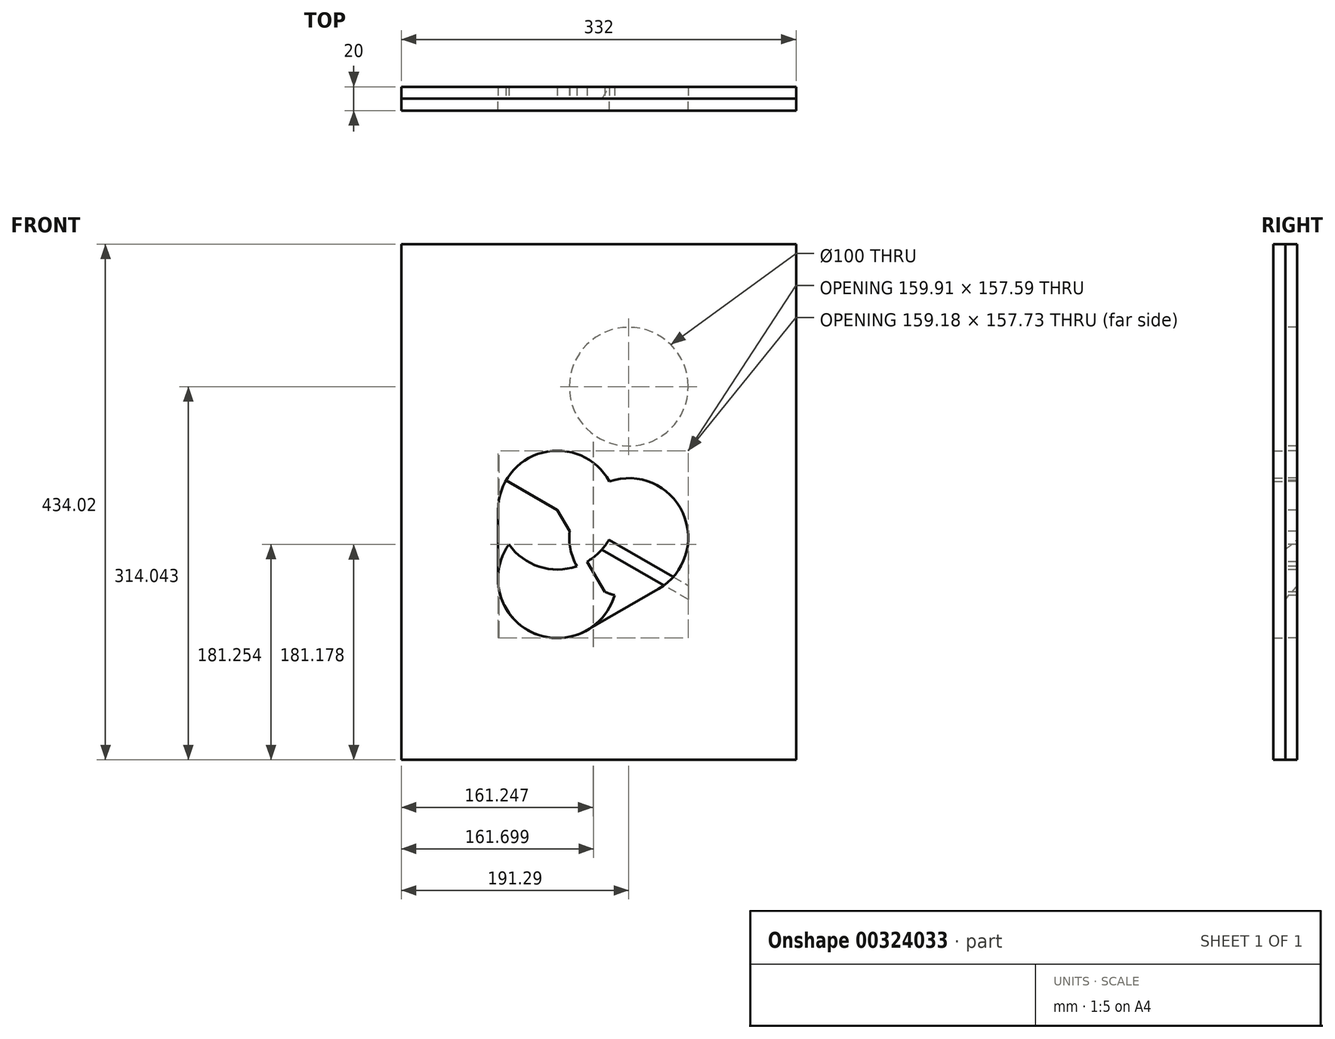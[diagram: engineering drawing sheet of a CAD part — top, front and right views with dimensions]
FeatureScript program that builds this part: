
annotation { "Feature Type Name" : "Feature", "Feature Type Description" : "" }
export const myFeature = defineFeature(function(context is Context, id is Id, definition is map)
    precondition{}
    {
        {
            var Q0;
            Q0=qCreatedBy(makeId("Front.planeOp"),FACE);
            var sketch = newSketch(context, id + "F0", { "sketchPlane" : qUnion([Q0])});
            skCircle(sketch, "E0", {"center": v(0, 0) * mm, "radius": 50 * mm});
            skCircle(sketch, "E1", {"center": v(0, -57.74) * mm, "radius": 50 * mm});
            skCircle(sketch, "E2", {"center": v(60, -23.1) * mm, "radius": 50 * mm});
            skLineSegment(sketch, "E3", {"start": v(0, 0) * mm, "end": v(50, -86.6) * mm});
            skLineSegment(sketch, "E4", {"start": v(50, -86.6) * mm, "end": v(85, -66.4) * mm});
            skLineSegment(sketch, "E5", {"start": v(50, -86.6) * mm, "end": v(25, -101.04) * mm});
            skLineSegment(sketch, "E6", {"start": v(-50, 0) * mm, "end": v(-50, -57.74) * mm});
            skLineSegment(sketch, "E7", {"start": v(-50, -57.74) * mm, "end": v(50, -57.74) * mm, "construction": true});
            skLineSegment(sketch, "E8", {"start": v(93.3, -61.6) * mm, "end": v(43.3, 25) * mm, "construction": true});
            skLineSegment(sketch, "E9", {"start": v(35, 20.2) * mm, "end": v(43.3, 25) * mm});
            skLineSegment(sketch, "E10", {"start": v(0, 0) * mm, "end": v(43.3, 25) * mm});
            skLineSegment(sketch, "E11", {"start": v(0, 0) * mm, "end": v(-43.3, 25) * mm});
            skLineSegment(sketch, "E12", {"start": v(-43.3, 25) * mm, "end": v(16.7, 128.92) * mm});
            skCircle(sketch, "E13", {"center": v(60, 103.92) * mm, "radius": 50 * mm});
            skLineSegment(sketch, "E14", {"start": v(0, 0) * mm, "end": v(43.3, -25) * mm});
            skLineSegment(sketch, "E15", {"start": v(43.3, -25) * mm, "end": v(110, -63.5) * mm});
            skLineSegment(sketch, "E16", {"start": v(110, 103.92) * mm, "end": v(110, -63.5) * mm});
            skLineSegment(sketch, "E17.bottom", {"start": v(-131.3, 223.9) * mm, "end": v(200.71, 223.9) * mm});
            skLineSegment(sketch, "E17.top", {"start": v(-131.3, -210.12) * mm, "end": v(200.71, -210.12) * mm});
            skLineSegment(sketch, "E17.left", {"start": v(-131.3, 223.9) * mm, "end": v(-131.3, -210.12) * mm});
            skLineSegment(sketch, "E17.right", {"start": v(200.71, 223.9) * mm, "end": v(200.71, -210.12) * mm});
            skSolve(sketch);
        }
        {
            var Q0;
            {var subQ5=sQuery(id+"F0.wireOp",EDGE,"E4");Q0=makeQuery(id+"F0.imprint","IMPRINT",FACE,{"disambiguationData":[TD([[makeQuery(id+"F0.imprint","IMPRINT",EDGE,{"derivedFrom":subQ5}),-1.0]])]});}
            var Q1;
            {var subQ0=sQuery(id+"F0.wireOp",EDGE,"E6");Q1=makeQuery(id+"F0.imprint","IMPRINT",FACE,{"disambiguationData":[TD([[makeQuery(id+"F0.imprint","IMPRINT",EDGE,{"derivedFrom":subQ0}),1.0]])]});}
            var Q2;
            {var subQ0=sQuery(id+"F0.wireOp",EDGE,"E1");var subQ5=sQuery(id+"F0.wireOp",EDGE,"E0");var subQ6=makeQuery(id+"F0.imprint","INTERSECT",VERTEX,{"disambiguationData":[OD(0.0)],"derivedFrom":[subQ5,subQ0]});Q2=makeQuery(id+"F0.imprint","IMPRINT",FACE,{"disambiguationData":[TD([[makeQuery(id+"F0.imprint","IMPRINT",EDGE,{"disambiguationData":[TD([[subQ6,-1.0]])],"derivedFrom":subQ5}),-1.0]])]});}
            var Q3;
            {var subQ0=sQuery(id+"F0.wireOp",EDGE,"E2");var subQ1=sQuery(id+"F0.wireOp",EDGE,"E0");var subQ2=makeQuery(id+"F0.imprint","INTERSECT",VERTEX,{"disambiguationData":[OD(1.0)],"derivedFrom":[subQ1,subQ0]});Q3=makeQuery(id+"F0.imprint","IMPRINT",FACE,{"disambiguationData":[TD([[makeQuery(id+"F0.imprint","IMPRINT",EDGE,{"disambiguationData":[TD([[subQ2,-1.0]])],"derivedFrom":subQ1}),-1.0]])]});}
            var Q4;
            {var subQ0=sQuery(id+"F0.wireOp",EDGE,"E3");var subQ1=sQuery(id+"F0.wireOp",EDGE,"E1");var subQ2=makeQuery(id+"F0.imprint","INTERSECT",VERTEX,{"disambiguationData":[OD(1.0)],"derivedFrom":[subQ1,subQ0]});Q4=makeQuery(id+"F0.imprint","IMPRINT",FACE,{"disambiguationData":[TD([[makeQuery(id+"F0.imprint","IMPRINT",EDGE,{"disambiguationData":[TD([[subQ2,-1.0]])],"derivedFrom":subQ1}),1.0]])]});}
            var Q5;
            {var subQ0=sQuery(id+"F0.wireOp",EDGE,"E3");var subQ1=sQuery(id+"F0.wireOp",EDGE,"E0");var subQ2=makeQuery(id+"F0.imprint","INTERSECT",VERTEX,{"derivedFrom":[subQ1,subQ0]});Q5=makeQuery(id+"F0.imprint","IMPRINT",FACE,{"disambiguationData":[TD([[makeQuery(id+"F0.imprint","IMPRINT",EDGE,{"disambiguationData":[TD([[subQ2,-1.0]])],"derivedFrom":subQ1}),-1.0]])]});}
            var Q6;
            {var subQ4=sQuery(id+"F0.wireOp",EDGE,"E1");var subQ5=sQuery(id+"F0.wireOp",EDGE,"E0");var subQ6=makeQuery(id+"F0.imprint","INTERSECT",VERTEX,{"disambiguationData":[OD(1.0)],"derivedFrom":[subQ5,subQ4]});Q6=makeQuery(id+"F0.imprint","IMPRINT",FACE,{"disambiguationData":[TD([[makeQuery(id+"F0.imprint","IMPRINT",EDGE,{"disambiguationData":[TD([[subQ6,1.0]])],"derivedFrom":subQ4}),-1.0]])]});}
            var Q7;
            {var subQ5=sQuery(id+"F0.wireOp",EDGE,"E4");Q7=makeQuery(id+"F0.imprint","IMPRINT",FACE,{"disambiguationData":[TD([[makeQuery(id+"F0.imprint","IMPRINT",EDGE,{"derivedFrom":subQ5}),1.0]])]});}
            var Q8;
            {var subQ0=sQuery(id+"F0.wireOp",EDGE,"E5");Q8=makeQuery(id+"F0.imprint","IMPRINT",FACE,{"disambiguationData":[TD([[makeQuery(id+"F0.imprint","IMPRINT",EDGE,{"derivedFrom":subQ0}),-1.0]])]});}
            extrude(context, id + "F1", {"entities" : qUnion([Q0, Q1, Q2, Q3, Q4, Q5, Q6, Q7, Q8]), "depth" : -10 * mm});
        }
        {
            var Q0;
            {var subQ0=sQuery(id+"F0.wireOp",EDGE,"E12");Q0=makeQuery(id+"F0.imprint","IMPRINT",FACE,{"disambiguationData":[TD([[makeQuery(id+"F0.imprint","IMPRINT",EDGE,{"derivedFrom":subQ0}),-1.0]])]});}
            var Q1;
            {var subQ5=sQuery(id+"F0.wireOp",EDGE,"E4");Q1=makeQuery(id+"F0.imprint","IMPRINT",FACE,{"disambiguationData":[TD([[makeQuery(id+"F0.imprint","IMPRINT",EDGE,{"derivedFrom":subQ5}),-1.0]])]});}
            var Q2;
            {var subQ0=sQuery(id+"F0.wireOp",EDGE,"E13");var subQ1=makeQuery(id+"F0.imprint","INTERSECT",VERTEX,{"derivedFrom":[sQuery(id+"F0.wireOp",EDGE,"E12"),subQ0]});Q2=makeQuery(id+"F0.imprint","IMPRINT",FACE,{"disambiguationData":[TD([[makeQuery(id+"F0.imprint","IMPRINT",EDGE,{"disambiguationData":[TD([[subQ1,1.0]])],"derivedFrom":subQ0}),1.0]])]});}
            var Q3;
            {var subQ0=sQuery(id+"F0.wireOp",EDGE,"E16");var subQ1=sQuery(id+"F0.wireOp",EDGE,"E2");var subQ2=makeQuery(id+"F0.imprint","INTERSECT",VERTEX,{"derivedFrom":[subQ1,subQ0]});Q3=makeQuery(id+"F0.imprint","IMPRINT",FACE,{"disambiguationData":[TD([[makeQuery(id+"F0.imprint","IMPRINT",EDGE,{"disambiguationData":[TD([[subQ2,1.0]])],"derivedFrom":subQ1}),-1.0]])]});}
            extrude(context, id + "F2", {"entities" : qUnion([Q0, Q1, Q2, Q3]), "depth" : 10 * mm});
        }
        {
            var Q0;
            Q0=makeQuery(id+"F1.opExtrude","CAP_EDGE",EDGE,{"disambiguationData":[OSD([sQuery(id+"F0.wireOp",EDGE,"E15")])],"isStart":true});
            chamfer(context, id + "F3", {"entities" : qUnion([Q0]), "width" : 10 * mm, "tangentPropagation" : true});
        }
    });
